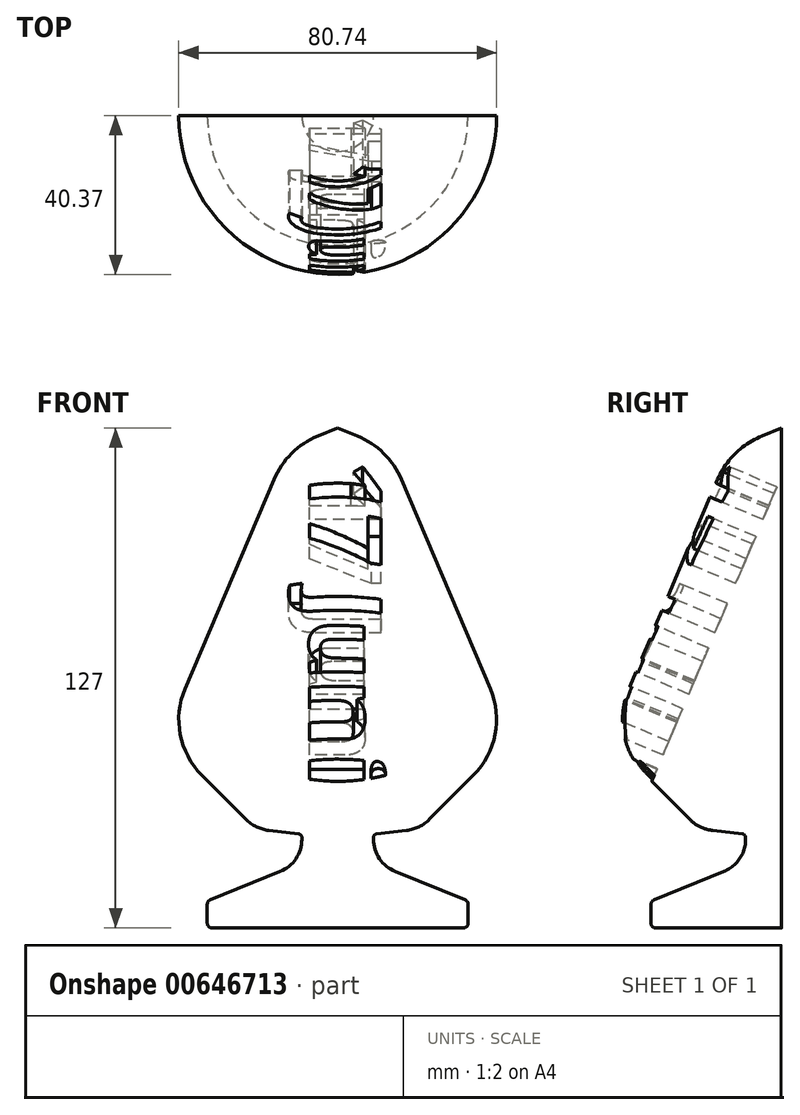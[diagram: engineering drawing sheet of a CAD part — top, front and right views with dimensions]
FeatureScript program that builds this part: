
annotation { "Feature Type Name" : "Feature", "Feature Type Description" : "" }
export const myFeature = defineFeature(function(context is Context, id is Id, definition is map)
    precondition{}
    {
        {
            var Q0;
            Q0=qCreatedBy(makeId("Right.planeOp"),FACE);
            var sketch = newSketch(context, id + "F0", { "sketchPlane" : qUnion([Q0])});
            skLineSegment(sketch, "E0", {"start": v(0, 104.47) * mm, "end": v(-5.01, 102.43) * mm});
            skLineSegment(sketch, "E1", {"start": v(-16.22, 91.38) * mm, "end": v(-38.78, 38.23) * mm});
            skLineSegment(sketch, "E2", {"start": v(-17.47, 2.22) * mm, "end": v(-9.9, 1.33) * mm});
            skLineSegment(sketch, "E3", {"start": v(-9.1, 0.42) * mm, "end": v(-9.1, 0) * mm});
            skLineSegment(sketch, "E4", {"start": v(-14.61, -8.2) * mm, "end": v(-32.42, -15.44) * mm});
            skLineSegment(sketch, "E5", {"start": v(-33.13, -16.48) * mm, "end": v(-33.13, -21.4) * mm});
            skLineSegment(sketch, "E6", {"start": v(-32, -22.53) * mm, "end": v(0, -22.53) * mm});
            skPoint(sketch, "E7.visualSharp", {"position": v(-12.9, 99.22) * mm});
            skArc(sketch, "E7.filletArc", {"start": v(-5.01, 102.43) * mm, "mid": v(-11.7, 98.02) * mm, "end": v(-16.22, 91.38) * mm});
            skPoint(sketch, "E8.visualSharp", {"position": v(-52.32, 6.32) * mm});
            skPoint(sketch, "E9.visualSharp", {"position": v(-9.1, 1.24) * mm});
            skArc(sketch, "E9.filletArc", {"start": v(-9.1, 0.42) * mm, "mid": v(-9.33, 1.03) * mm, "end": v(-9.9, 1.33) * mm});
            skPoint(sketch, "E10.visualSharp", {"position": v(-9.1, -5.96) * mm});
            skArc(sketch, "E10.filletArc", {"start": v(-14.61, -8.2) * mm, "mid": v(-10.6, -4.94) * mm, "end": v(-9.1, 0) * mm});
            skPoint(sketch, "E11.visualSharp", {"position": v(-33.13, -15.72) * mm});
            skArc(sketch, "E11.filletArc", {"start": v(-32.42, -15.44) * mm, "mid": v(-32.93, -15.85) * mm, "end": v(-33.13, -16.48) * mm});
            skPoint(sketch, "E12.visualSharp", {"position": v(-33.13, -22.53) * mm});
            skArc(sketch, "E12.filletArc", {"start": v(-33.13, -21.4) * mm, "mid": v(-32.8, -22.2) * mm, "end": v(-32, -22.53) * mm});
            skLineSegment(sketch, "E13", {"start": v(0, 104.47) * mm, "end": v(0, -22.53) * mm});
            skLineSegment(sketch, "E14", {"start": v(0, 73.32) * mm, "end": v(0, -47.2) * mm, "construction": true});
            skLineSegment(sketch, "E15", {"start": v(-34.54, 16.3) * mm, "end": v(-23.38, 5.1) * mm});
            skPoint(sketch, "E16.visualSharp", {"position": v(-44.04, 25.83) * mm});
            skArc(sketch, "E16.filletArc", {"start": v(-38.78, 38.23) * mm, "mid": v(-40, 26.61) * mm, "end": v(-34.54, 16.3) * mm});
            skPoint(sketch, "E17.visualSharp", {"position": v(-20.92, 2.63) * mm});
            skArc(sketch, "E17.filletArc", {"start": v(-23.38, 5.1) * mm, "mid": v(-20.67, 3.16) * mm, "end": v(-17.47, 2.22) * mm});
            skSolve(sketch);
        }
        {
            var Q0;
            Q0 = qSketchRegion(id + "F0", true);
            var Q1;
            Q1=sQuery(id+"F0.wireOp",EDGE,"E14");
            revolve(context, id + "F1", {"entities" : qUnion([Q0]), "axis" : qUnion([Q1]), "revolveType" : RevolveType.SYMMETRIC, "angle" : 180 * degree});
        }
        {
            var Q0;
            Q0=qCreatedBy(makeId("Right.planeOp"),FACE);
            var sketch = newSketch(context, id + "F2", { "sketchPlane" : qUnion([Q0])});
            skLineSegment(sketch, "E18", {"start": v(-37.63, 29.28) * mm, "end": v(-8.37, 98.18) * mm, "construction": true});
            skSolve(sketch);
        }
        {
            var Q0;
            Q0=sQuery(id+"F2.wireOp",EDGE,"E18");
            cPlane(context, id + "F3", {"entities" : qUnion([Q0]), "cplaneType" : CPlaneType.LINE_ANGLE, "offset" : 25 * mm, "angle" : 270 * degree, "width" : 150 * mm, "height" : 150 * mm});
        }
        {
            var Q0;
            Q0=qCreatedBy(id+"F3.planeOp",FACE);
            var sketch = newSketch(context, id + "F4", { "sketchPlane" : qUnion([Q0])});
            skText(sketch, "E19", { "text": "17 Juni", "fontName": "OpenSans-Bold.ttf"});
            const initialGuessF4  = {"E19": [-0.00715, 0.08343, 0, -1, 0.0183]};
            skSetInitialGuess(sketch, initialGuessF4);
            skSolve(sketch);
        }
        {
            var Q0;
            Q0 = qSketchRegion(id + "F4", true);
            extrude(context, id + "F5", {"entities" : qUnion([Q0]), "operationType" : NewBodyOperationType.REMOVE, "oppositeDirection" : true, "depth" : 10 * mm, "offsetDistance" : 25 * mm, "hasSecondDirection" : true, "secondDirectionOppositeDirection" : false, "secondDirectionDepth" : 25 * mm});
        }
    });
